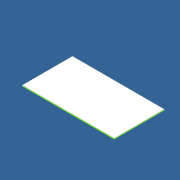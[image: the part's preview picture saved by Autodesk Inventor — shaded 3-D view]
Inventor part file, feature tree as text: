
AUTODESK INVENTOR PART (.ipt)
format: ipt  version: unknown  size: 4,349,952 bytes
history: native  units: mm
features: sketch x7, other x6, extrude x1
ambient origin geometry x8: Origin, YZ Plane, XZ Plane, XY Plane, X Axis, Y Axis, Z Axis, Center Point
feature tree (14):
  sketch  "Эскиз1"
  extrude  "Выдавливание1"  Depth=55.0mm
  other  "Рельеф2"
  other  "Рельеф3"
  sketch  "Эскиз10"
  other  "Рельеф4"
  other  "Рельеф6"
  other  "Рельеф7"
  other  "Рельеф10"
  sketch  "Эскиз8"
  sketch  "Эскиз9"
  sketch  "Эскиз11"
  sketch  "Эскиз13"
  sketch  "Эскиз16"
